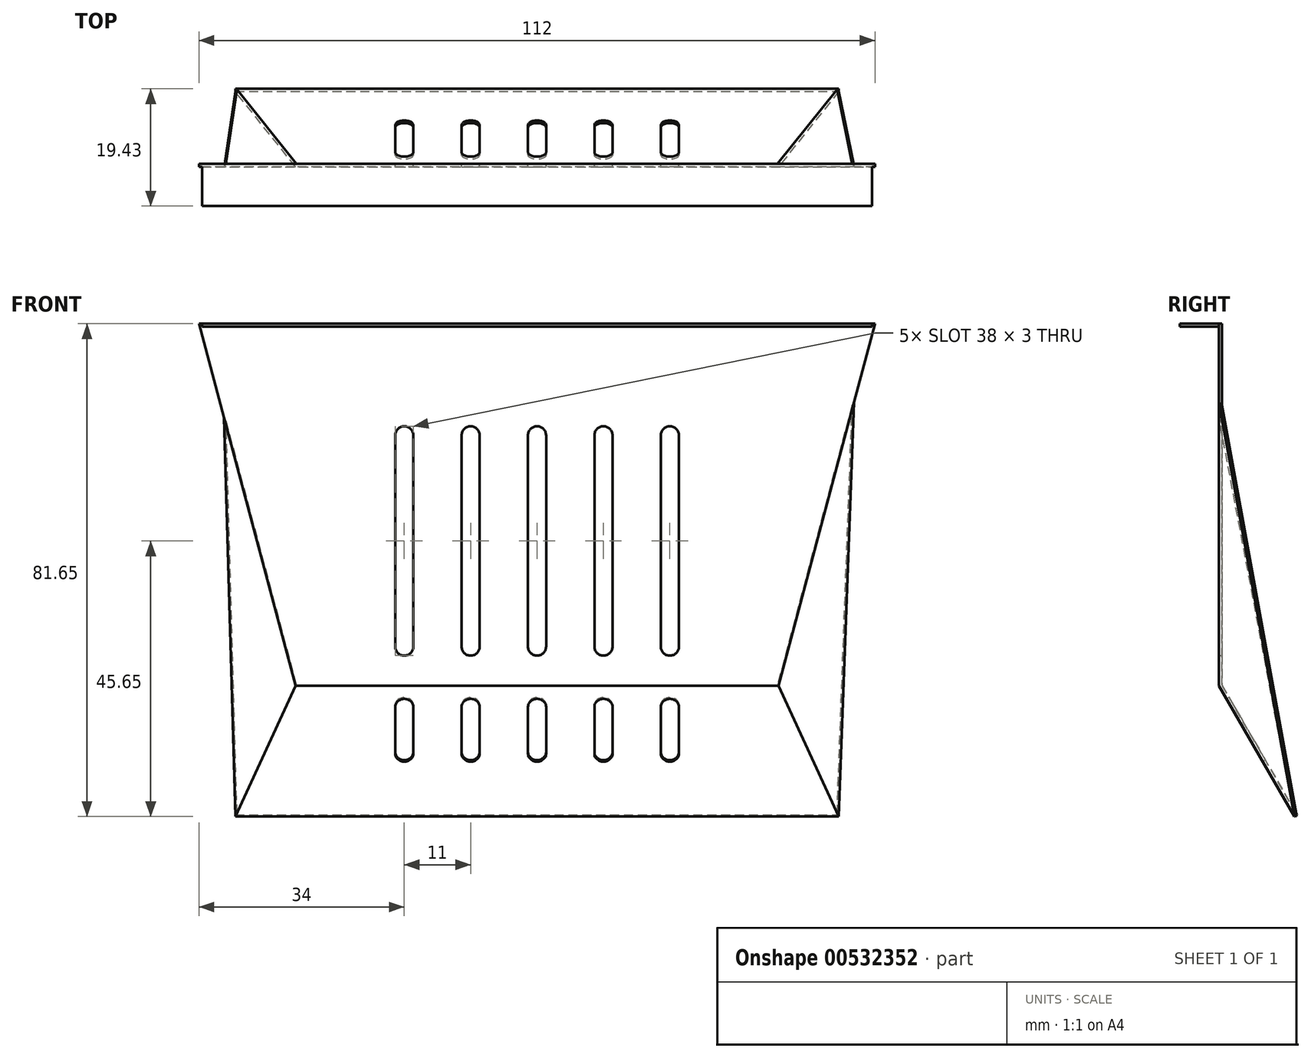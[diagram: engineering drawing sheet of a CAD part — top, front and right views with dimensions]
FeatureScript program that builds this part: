
annotation { "Feature Type Name" : "Feature", "Feature Type Description" : "" }
export const myFeature = defineFeature(function(context is Context, id is Id, definition is map)
    precondition{}
    {
        {
            var Q0;
            Q0=qCreatedBy(makeId("Front.planeOp"),FACE);
            var sketch = newSketch(context, id + "F0", { "sketchPlane" : qUnion([Q0])});
            skLineSegment(sketch, "E0", {"start": v(40, 0) * mm, "end": v(-40, 0) * mm});
            skLineSegment(sketch, "E1", {"start": v(-40, 0) * mm, "end": v(-56, 60) * mm});
            skLineSegment(sketch, "E2", {"start": v(-56, 60) * mm, "end": v(56, 60) * mm});
            skLineSegment(sketch, "E3", {"start": v(56, 60) * mm, "end": v(40, 0) * mm});
            skLineSegment(sketch, "E4.left", {"start": v(20.5, 41.5) * mm, "end": v(20.5, 6.5) * mm});
            skLineSegment(sketch, "E4.right", {"start": v(23.5, 41.5) * mm, "end": v(23.5, 6.5) * mm});
            skArc(sketch, "E5", {"start": v(20.5, 41.5) * mm, "mid": v(22, 43) * mm, "end": v(23.5, 41.5) * mm});
            skArc(sketch, "E6", {"start": v(23.5, 6.5) * mm, "mid": v(22, 5) * mm, "end": v(20.5, 6.5) * mm});
            skArc(sketch, "E7.1.0.0", {"start": v(12.5, 6.5) * mm, "mid": v(11, 5) * mm, "end": v(9.5, 6.5) * mm});
            skLineSegment(sketch, "E7.1.0.1", {"start": v(12.5, 41.5) * mm, "end": v(12.5, 6.5) * mm});
            skArc(sketch, "E7.1.0.2", {"start": v(9.5, 41.5) * mm, "mid": v(11, 43) * mm, "end": v(12.5, 41.5) * mm});
            skLineSegment(sketch, "E7.1.0.3", {"start": v(9.5, 41.5) * mm, "end": v(9.5, 6.5) * mm});
            skArc(sketch, "E7.2.0.0", {"start": v(1.5, 6.5) * mm, "mid": v(0, 5) * mm, "end": v(-1.5, 6.5) * mm});
            skLineSegment(sketch, "E7.2.0.1", {"start": v(1.5, 41.5) * mm, "end": v(1.5, 6.5) * mm});
            skArc(sketch, "E7.2.0.2", {"start": v(-1.5, 41.5) * mm, "mid": v(0, 43) * mm, "end": v(1.5, 41.5) * mm});
            skLineSegment(sketch, "E7.2.0.3", {"start": v(-1.5, 41.5) * mm, "end": v(-1.5, 6.5) * mm});
            skArc(sketch, "E7.3.0.0", {"start": v(-9.5, 6.5) * mm, "mid": v(-11, 5) * mm, "end": v(-12.5, 6.5) * mm});
            skLineSegment(sketch, "E7.3.0.1", {"start": v(-9.5, 41.5) * mm, "end": v(-9.5, 6.5) * mm});
            skArc(sketch, "E7.3.0.2", {"start": v(-12.5, 41.5) * mm, "mid": v(-11, 43) * mm, "end": v(-9.5, 41.5) * mm});
            skLineSegment(sketch, "E7.3.0.3", {"start": v(-12.5, 41.5) * mm, "end": v(-12.5, 6.5) * mm});
            skArc(sketch, "E7.4.0.0", {"start": v(-20.5, 6.5) * mm, "mid": v(-22, 5) * mm, "end": v(-23.5, 6.5) * mm});
            skLineSegment(sketch, "E7.4.0.1", {"start": v(-20.5, 41.5) * mm, "end": v(-20.5, 6.5) * mm});
            skArc(sketch, "E7.4.0.2", {"start": v(-23.5, 41.5) * mm, "mid": v(-22, 43) * mm, "end": v(-20.5, 41.5) * mm});
            skLineSegment(sketch, "E7.4.0.3", {"start": v(-23.5, 41.5) * mm, "end": v(-23.5, 6.5) * mm});
            skLineSegment(sketch, "E7.direction1", {"start": v(20.5, 6.5) * mm, "end": v(9.5, 6.5) * mm, "construction": true});
            skSolve(sketch);
        }
        {
            var Q0;
            Q0=makeQuery(id+"F0.imprint","IMPRINT",FACE,{"disambiguationData":[TD([[makeQuery(id+"F0.imprint","IMPRINT",EDGE,{"derivedFrom":sQuery(id+"F0.wireOp",EDGE,"E0")}),-1.0]])]});
            extrude(context, id + "F1", {"entities" : qUnion([Q0]), "depth" : 0.5 * mm});
        }
        {
            var Q0;
            Q0=makeQuery(id+"F1.opExtrude","CAP_FACE",FACE,{"disambiguationData":[OSD([sQuery(id+"F0.wireOp",EDGE,"E0"),sQuery(id+"F0.wireOp",EDGE,"E1"),sQuery(id+"F0.wireOp",EDGE,"E2"),sQuery(id+"F0.wireOp",EDGE,"E3"),sQuery(id+"F0.wireOp",EDGE,"E4.left"),sQuery(id+"F0.wireOp",EDGE,"E4.right"),sQuery(id+"F0.wireOp",EDGE,"E5"),sQuery(id+"F0.wireOp",EDGE,"E6"),sQuery(id+"F0.wireOp",EDGE,"E7.1.0.0"),sQuery(id+"F0.wireOp",EDGE,"E7.1.0.1"),sQuery(id+"F0.wireOp",EDGE,"E7.1.0.2"),sQuery(id+"F0.wireOp",EDGE,"E7.1.0.3"),sQuery(id+"F0.wireOp",EDGE,"E7.2.0.0"),sQuery(id+"F0.wireOp",EDGE,"E7.2.0.1"),sQuery(id+"F0.wireOp",EDGE,"E7.2.0.2"),sQuery(id+"F0.wireOp",EDGE,"E7.2.0.3"),sQuery(id+"F0.wireOp",EDGE,"E7.3.0.0"),sQuery(id+"F0.wireOp",EDGE,"E7.3.0.1"),sQuery(id+"F0.wireOp",EDGE,"E7.3.0.2"),sQuery(id+"F0.wireOp",EDGE,"E7.3.0.3"),sQuery(id+"F0.wireOp",EDGE,"E7.4.0.0"),sQuery(id+"F0.wireOp",EDGE,"E7.4.0.1"),sQuery(id+"F0.wireOp",EDGE,"E7.4.0.2"),sQuery(id+"F0.wireOp",EDGE,"E7.4.0.3")])],"isStart":false});
            var sketch = newSketch(context, id + "F2", { "sketchPlane" : qUnion([Q0])});
            skLineSegment(sketch, "E8.0", {"start": v(-55.5, 60) * mm, "end": v(55.5, 60) * mm});
            skLineSegment(sketch, "E9", {"start": v(-55.5, 60) * mm, "end": v(-55.5, 59.5) * mm});
            skLineSegment(sketch, "E10", {"start": v(-55.5, 59.5) * mm, "end": v(55.5, 59.5) * mm});
            skLineSegment(sketch, "E11", {"start": v(55.5, 59.5) * mm, "end": v(55.5, 60) * mm});
            skPoint(sketch, "E12.orphan", {"position": v(56, 60) * mm});
            skPoint(sketch, "E13.orphan", {"position": v(-56, 60) * mm});
            skSolve(sketch);
        }
        {
            var Q0;
            Q0=qSketchRegion(id+"F2",true);
            extrude(context, id + "F3", {"entities" : qUnion([Q0]), "operationType" : NewBodyOperationType.ADD, "depth" : 6.5 * mm});
        }
        {
            var Q0;
            Q0=makeQuery(id+"F1.opExtrude","CAP_EDGE",EDGE,{"disambiguationData":[OSD([sQuery(id+"F0.wireOp",EDGE,"E0")])],"isStart":false});
            cPlane(context, id + "F4", {"entities" : qUnion([Q0]), "cplaneType" : CPlaneType.LINE_ANGLE, "offset" : 25 * mm, "angle" : 30 * degree, "oppositeDirection" : true, "width" : 150 * mm, "height" : 150 * mm});
        }
        {
            var Q0;
            Q0=qCreatedBy(id+"F4.planeOp",FACE);
            var sketch = newSketch(context, id + "F5", { "sketchPlane" : qUnion([Q0])});
            skLineSegment(sketch, "E14.0", {"start": v(40, 0.25) * mm, "end": v(-40, 0.25) * mm});
            skLineSegment(sketch, "E15", {"start": v(-40, 0.25) * mm, "end": v(-50, -24.75) * mm});
            skLineSegment(sketch, "E16", {"start": v(-50, -24.75) * mm, "end": v(50, -24.75) * mm});
            skLineSegment(sketch, "E17", {"start": v(50, -24.75) * mm, "end": v(40, 0.25) * mm});
            skLineSegment(sketch, "E18.bottom", {"start": v(-23.5, -3.75) * mm, "end": v(-20.5, -3.75) * mm});
            skLineSegment(sketch, "E18.top", {"start": v(-23.5, -12.75) * mm, "end": v(-20.5, -12.75) * mm});
            skLineSegment(sketch, "E18.left", {"start": v(-23.5, -3.75) * mm, "end": v(-23.5, -12.75) * mm});
            skLineSegment(sketch, "E18.right", {"start": v(-20.5, -3.75) * mm, "end": v(-20.5, -12.75) * mm});
            skArc(sketch, "E19", {"start": v(-23.5, -3.75) * mm, "mid": v(-22, -2.25) * mm, "end": v(-20.5, -3.75) * mm});
            skArc(sketch, "E20", {"start": v(-20.5, -12.75) * mm, "mid": v(-22, -14.25) * mm, "end": v(-23.5, -12.75) * mm});
            skLineSegment(sketch, "E21.1.0.0", {"start": v(-12.5, -12.75) * mm, "end": v(-9.5, -12.75) * mm});
            skLineSegment(sketch, "E21.1.0.1", {"start": v(-12.5, -3.75) * mm, "end": v(-9.5, -3.75) * mm});
            skLineSegment(sketch, "E21.1.0.2", {"start": v(-12.5, -3.75) * mm, "end": v(-12.5, -12.75) * mm});
            skLineSegment(sketch, "E21.1.0.3", {"start": v(-9.5, -3.75) * mm, "end": v(-9.5, -12.75) * mm});
            skArc(sketch, "E21.1.0.4", {"start": v(-12.5, -3.75) * mm, "mid": v(-11, -2.25) * mm, "end": v(-9.5, -3.75) * mm});
            skArc(sketch, "E21.1.0.5", {"start": v(-9.5, -12.75) * mm, "mid": v(-11, -14.25) * mm, "end": v(-12.5, -12.75) * mm});
            skLineSegment(sketch, "E21.2.0.0", {"start": v(-1.5, -12.75) * mm, "end": v(1.5, -12.75) * mm});
            skLineSegment(sketch, "E21.2.0.1", {"start": v(-1.5, -3.75) * mm, "end": v(1.5, -3.75) * mm});
            skLineSegment(sketch, "E21.2.0.2", {"start": v(-1.5, -3.75) * mm, "end": v(-1.5, -12.75) * mm});
            skLineSegment(sketch, "E21.2.0.3", {"start": v(1.5, -3.75) * mm, "end": v(1.5, -12.75) * mm});
            skArc(sketch, "E21.2.0.4", {"start": v(-1.5, -3.75) * mm, "mid": v(0, -2.25) * mm, "end": v(1.5, -3.75) * mm});
            skArc(sketch, "E21.2.0.5", {"start": v(1.5, -12.75) * mm, "mid": v(0, -14.25) * mm, "end": v(-1.5, -12.75) * mm});
            skLineSegment(sketch, "E21.3.0.0", {"start": v(9.5, -12.75) * mm, "end": v(12.5, -12.75) * mm});
            skLineSegment(sketch, "E21.3.0.1", {"start": v(9.5, -3.75) * mm, "end": v(12.5, -3.75) * mm});
            skLineSegment(sketch, "E21.3.0.2", {"start": v(9.5, -3.75) * mm, "end": v(9.5, -12.75) * mm});
            skLineSegment(sketch, "E21.3.0.3", {"start": v(12.5, -3.75) * mm, "end": v(12.5, -12.75) * mm});
            skArc(sketch, "E21.3.0.4", {"start": v(9.5, -3.75) * mm, "mid": v(11, -2.25) * mm, "end": v(12.5, -3.75) * mm});
            skArc(sketch, "E21.3.0.5", {"start": v(12.5, -12.75) * mm, "mid": v(11, -14.25) * mm, "end": v(9.5, -12.75) * mm});
            skLineSegment(sketch, "E21.4.0.0", {"start": v(20.5, -12.75) * mm, "end": v(23.5, -12.75) * mm});
            skLineSegment(sketch, "E21.4.0.1", {"start": v(20.5, -3.75) * mm, "end": v(23.5, -3.75) * mm});
            skLineSegment(sketch, "E21.4.0.2", {"start": v(20.5, -3.75) * mm, "end": v(20.5, -12.75) * mm});
            skLineSegment(sketch, "E21.4.0.3", {"start": v(23.5, -3.75) * mm, "end": v(23.5, -12.75) * mm});
            skArc(sketch, "E21.4.0.4", {"start": v(20.5, -3.75) * mm, "mid": v(22, -2.25) * mm, "end": v(23.5, -3.75) * mm});
            skArc(sketch, "E21.4.0.5", {"start": v(23.5, -12.75) * mm, "mid": v(22, -14.25) * mm, "end": v(20.5, -12.75) * mm});
            skLineSegment(sketch, "E21.direction1", {"start": v(-23.5, -12.75) * mm, "end": v(-12.5, -12.75) * mm, "construction": true});
            skSolve(sketch);
        }
        {
            var Q0;
            Q0=makeQuery(id+"F5.imprint","IMPRINT",FACE,{"disambiguationData":[TD([[makeQuery(id+"F5.imprint","IMPRINT",EDGE,{"derivedFrom":sQuery(id+"F5.wireOp",EDGE,"E14.0")}),1.0]])]});
            extrude(context, id + "F6", {"entities" : qUnion([Q0]), "operationType" : NewBodyOperationType.ADD, "oppositeDirection" : true, "depth" : 0.5 * mm});
        }
        {
            var Q0;
            Q0=makeQuery(id+"F1.opExtrude","CAP_VERTEX",VERTEX,{"disambiguationData":[OSD([sQuery(id+"F0.wireOp",EDGE,"E2"),sQuery(id+"F0.wireOp",EDGE,"E3")])],"isStart":false});
            var Q1;
            Q1=makeQuery(id+"F6.boolean.opBoolean","MERGE",VERTEX,{"derivedFrom":[makeQuery(id+"F1.opExtrude","CAP_VERTEX",VERTEX,{"disambiguationData":[OSD([sQuery(id+"F0.wireOp",EDGE,"E0"),sQuery(id+"F0.wireOp",EDGE,"E3")])],"isStart":false}),makeQuery(id+"F6.opExtrude","CAP_VERTEX",VERTEX,{"disambiguationData":[OSD([sQuery(id+"F5.wireOp",EDGE,"E14.0"),sQuery(id+"F5.wireOp",EDGE,"E17")])],"isStart":true})]});
            var Q2;
            Q2=makeQuery(id+"F6.opExtrude","CAP_VERTEX",VERTEX,{"disambiguationData":[OSD([sQuery(id+"F5.wireOp",EDGE,"E16"),sQuery(id+"F5.wireOp",EDGE,"E17")])],"isStart":true});
            cPlane(context, id + "F7", {"entities" : qUnion([Q0, Q1, Q2]), "cplaneType" : CPlaneType.THREE_POINT, "offset" : 25 * mm, "width" : 150 * mm, "height" : 150 * mm});
        }
        {
            var Q0;
            Q0=qCreatedBy(id+"F7.planeOp",FACE);
            var sketch = newSketch(context, id + "F8", { "sketchPlane" : qUnion([Q0])});
            skLineSegment(sketch, "E22.0", {"start": v(-43.97, -23.66) * mm, "end": v(-31.31, 0.1) * mm});
            skLineSegment(sketch, "E23.0", {"start": v(-47.18, 46.1) * mm, "end": v(-31.31, 0.1) * mm});
            skLineSegment(sketch, "E24", {"start": v(-43.97, -23.66) * mm, "end": v(-47.18, 46.1) * mm});
            skPoint(sketch, "E25.orphan", {"position": v(-51.56, 58.8) * mm});
            skSolve(sketch);
        }
        {
            var Q0;
            Q0=makeQuery(id+"F8.imprint","IMPRINT",FACE,{"disambiguationData":[TD([[makeQuery(id+"F8.imprint","IMPRINT",EDGE,{"derivedFrom":sQuery(id+"F8.wireOp",EDGE,"E22.0")}),1.0]])]});
            extrude(context, id + "F9", {"entities" : qUnion([Q0]), "operationType" : NewBodyOperationType.ADD, "depth" : 0.5 * mm});
        }
        {
            var Q0;
            Q0=makeQuery(id+"F6.boolean.opBoolean","MERGE",VERTEX,{"derivedFrom":[makeQuery(id+"F1.opExtrude","CAP_VERTEX",VERTEX,{"disambiguationData":[OSD([sQuery(id+"F0.wireOp",EDGE,"E0"),sQuery(id+"F0.wireOp",EDGE,"E1")])],"isStart":false}),makeQuery(id+"F6.opExtrude","CAP_VERTEX",VERTEX,{"disambiguationData":[OSD([sQuery(id+"F5.wireOp",EDGE,"E14.0"),sQuery(id+"F5.wireOp",EDGE,"E15")])],"isStart":true})]});
            var Q1;
            Q1=makeQuery(id+"F1.opExtrude","CAP_VERTEX",VERTEX,{"disambiguationData":[OSD([sQuery(id+"F0.wireOp",EDGE,"E1"),sQuery(id+"F0.wireOp",EDGE,"E2")])],"isStart":false});
            var Q2;
            Q2=makeQuery(id+"F6.opExtrude","CAP_VERTEX",VERTEX,{"disambiguationData":[OSD([sQuery(id+"F5.wireOp",EDGE,"E15"),sQuery(id+"F5.wireOp",EDGE,"E16")])],"isStart":true});
            cPlane(context, id + "F10", {"entities" : qUnion([Q0, Q1, Q2]), "cplaneType" : CPlaneType.THREE_POINT, "offset" : 25 * mm, "width" : 150 * mm, "height" : 150 * mm});
        }
        {
            var Q0;
            Q0=qCreatedBy(id+"F10.planeOp",FACE);
            var sketch = newSketch(context, id + "F11", { "sketchPlane" : qUnion([Q0])});
            skLineSegment(sketch, "E26.0", {"start": v(31.31, 0.1) * mm, "end": v(43.97, -23.66) * mm});
            skLineSegment(sketch, "E26.1", {"start": v(31.31, 0.1) * mm, "end": v(46.3, 43.59) * mm});
            skLineSegment(sketch, "E27", {"start": v(43.97, -23.66) * mm, "end": v(46.3, 43.59) * mm});
            skPoint(sketch, "E28.orphan", {"position": v(51.56, 58.8) * mm});
            skSolve(sketch);
        }
        {
            var Q0;
            Q0=qSketchRegion(id+"F11",true);
            var Q1;
            Q1=sQuery(id+"F11.wireOp",EDGE,"E27");
            extrude(context, id + "F12", {"entities" : qUnion([Q0]), "operationType" : NewBodyOperationType.ADD, "surfaceEntities" : qUnion([Q1]), "depth" : 0.5 * mm});
        }
    });
